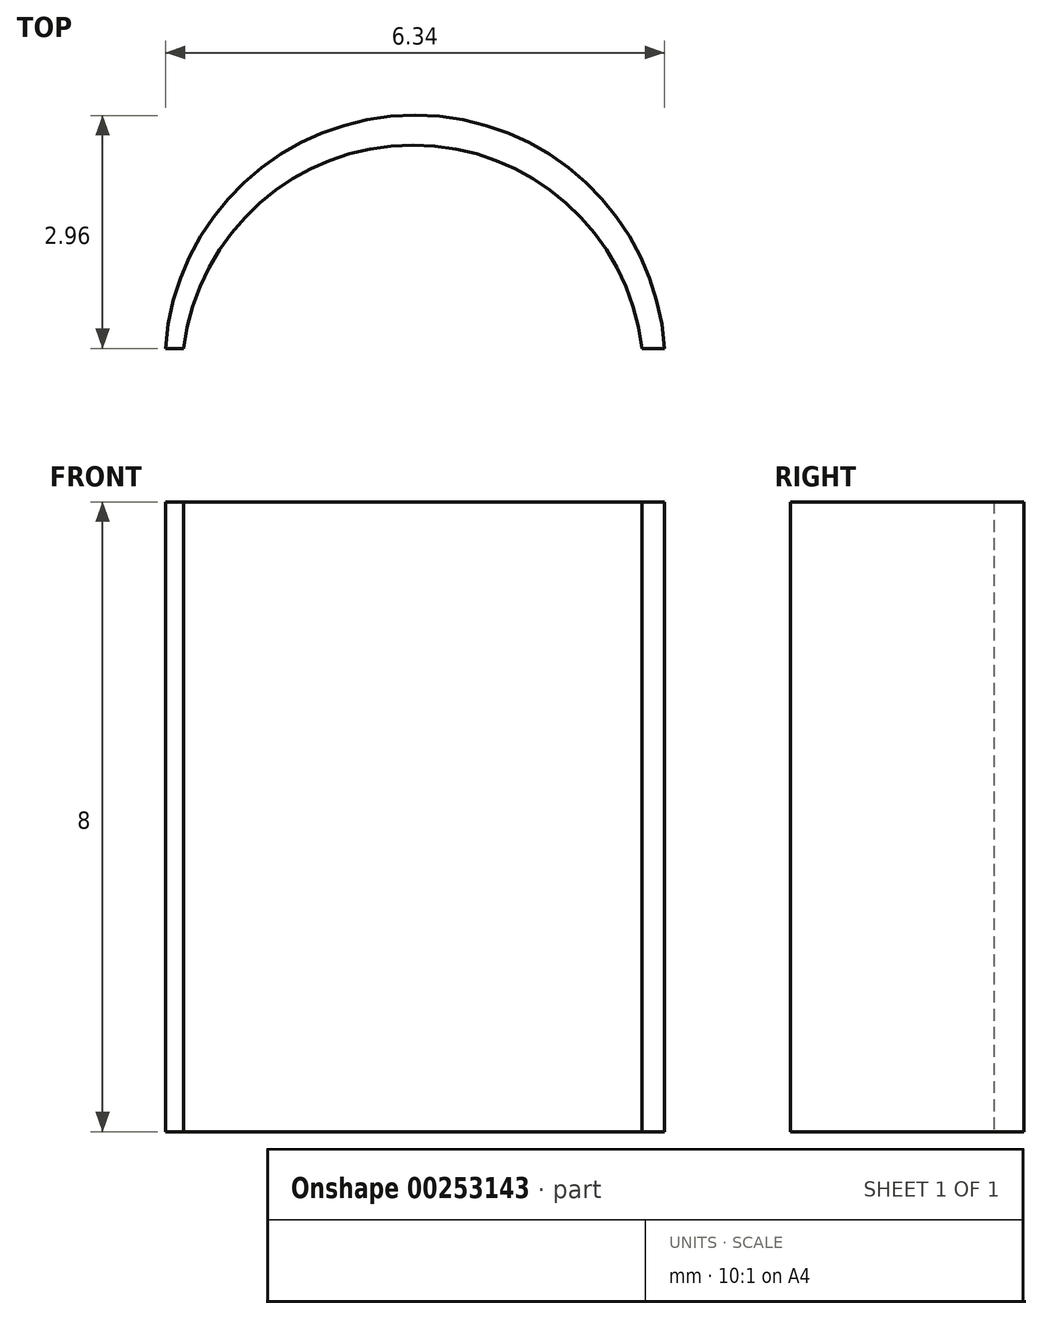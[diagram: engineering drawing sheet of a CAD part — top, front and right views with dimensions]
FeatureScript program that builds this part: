
annotation { "Feature Type Name" : "Feature", "Feature Type Description" : "" }
export const myFeature = defineFeature(function(context is Context, id is Id, definition is map)
    precondition{}
    {
        {
            var Q0;
            Q0=qCreatedBy(makeId("Top.planeOp"),FACE);
            var sketch = newSketch(context, id + "F0", { "sketchPlane" : qUnion([Q0])});
            skArc(sketch, "E0", {"start": v(-0.28, 0) * mm, "mid": v(-3.2, 2.58) * mm, "end": v(-6.1, 0) * mm});
            skLineSegment(sketch, "E1", {"start": v(-6.1, 0) * mm, "end": v(-6.34, 0) * mm});
            skLineSegment(sketch, "E2", {"start": v(-0.28, 0) * mm, "end": v(0, 0) * mm});
            skArc(sketch, "E3", {"start": v(0, 0) * mm, "mid": v(-3.17, 2.96) * mm, "end": v(-6.34, 0) * mm});
            skSolve(sketch);
        }
        {
            var Q0;
            Q0=makeQuery(id+"F0.imprint","IMPRINT",FACE,{"disambiguationData":[TD([[makeQuery(id+"F0.imprint","IMPRINT",EDGE,{"derivedFrom":sQuery(id+"F0.wireOp",EDGE,"E0")}),-1.0]])]});
            extrude(context, id + "F1", {"entities" : qUnion([Q0]), "depth" : 8 * mm});
        }
        {
            var Q0;
            Q0=makeQuery(id+"F1.opExtrude","SWEPT_BODY",BODY,{"disambiguationData":[OSD([sQuery(id+"F0.wireOp",EDGE,"E0"),sQuery(id+"F0.wireOp",EDGE,"E1"),sQuery(id+"F0.wireOp",EDGE,"E2"),sQuery(id+"F0.wireOp",EDGE,"E3")])]});
            transform(context, id + "F2", {"entities" : qUnion([Q0]), "transformType" : TransformType.TRANSLATION_3D, "dx" : 0 * mm, "dy" : 0 * mm, "dz" : 0 * mm, "makeCopy" : true});
        }
    });
